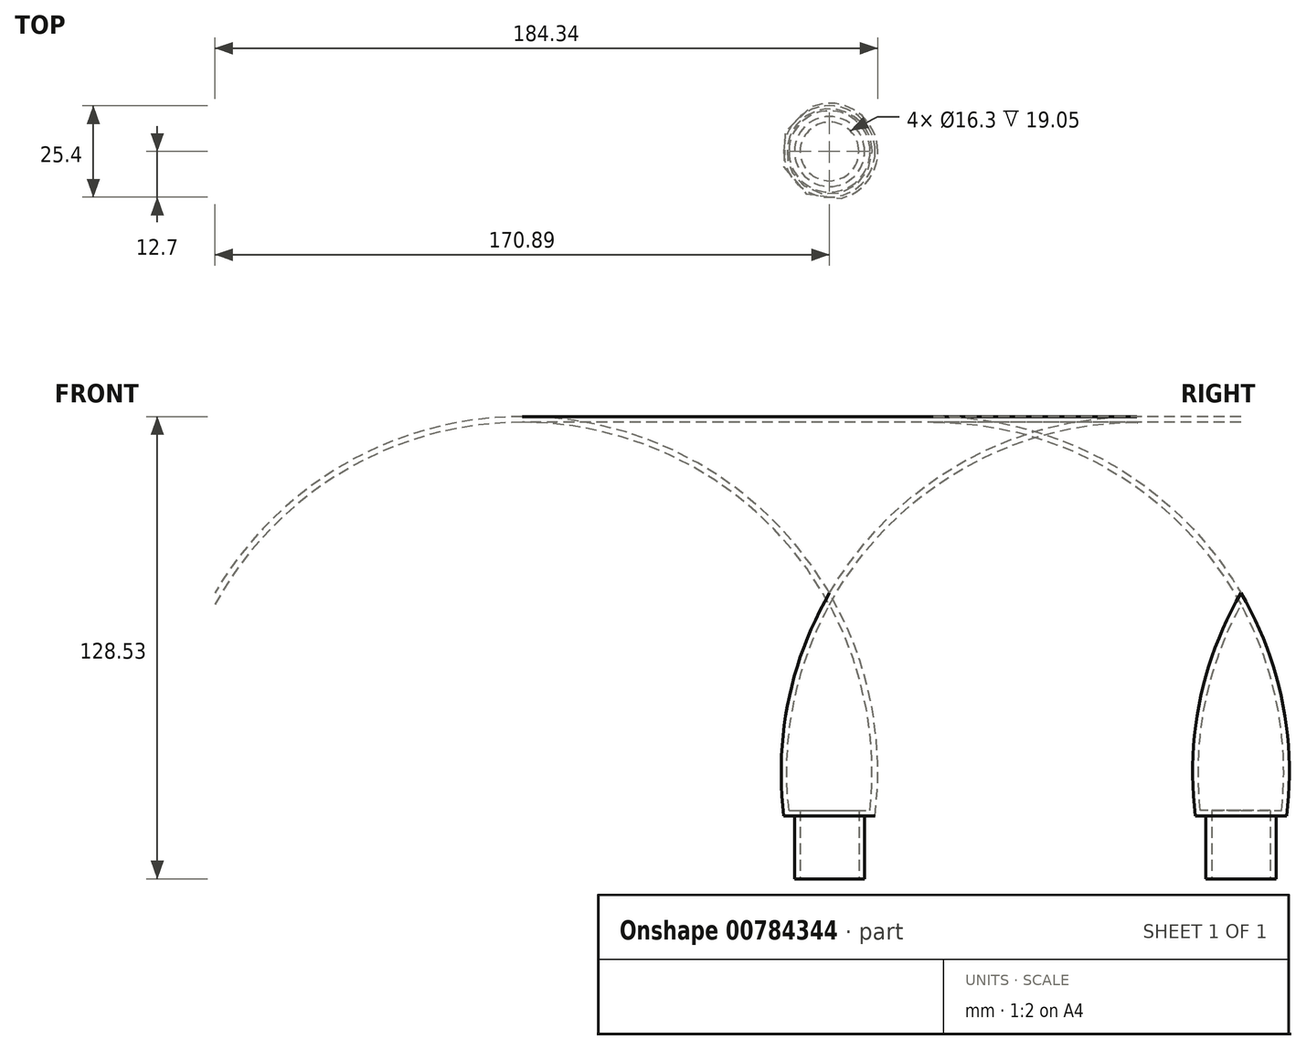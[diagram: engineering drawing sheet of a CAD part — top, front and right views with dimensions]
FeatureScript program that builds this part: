
annotation { "Feature Type Name" : "Feature", "Feature Type Description" : "" }
export const myFeature = defineFeature(function(context is Context, id is Id, definition is map)
    precondition{}
    {
        {
            var Q0;
            Q0=qCreatedBy(makeId("Front.planeOp"),FACE);
            var sketch = newSketch(context, id + "F0", { "sketchPlane" : qUnion([Q0])});
            skLineSegment(sketch, "E0", {"start": v(0, 0) * mm, "end": v(0, 76.2) * mm});
            skLineSegment(sketch, "E1", {"start": v(8.15, 0) * mm, "end": v(8.15, 19.05) * mm});
            skLineSegment(sketch, "E2", {"start": v(8.15, 19.05) * mm, "end": v(11.29, 19.05) * mm});
            skLineSegment(sketch, "E3", {"start": v(0, 76.2) * mm, "end": v(0, 79.43) * mm});
            skArc(sketch, "E4", {"start": v(11.29, 19.05) * mm, "mid": v(10.02, 48.49) * mm, "end": v(0, 76.2) * mm});
            skArc(sketch, "E5.0", {"start": v(12.7, 17.46) * mm, "mid": v(11.44, 49.5) * mm, "end": v(0, 79.43) * mm});
            skLineSegment(sketch, "E5.1", {"start": v(9.74, 17.46) * mm, "end": v(12.7, 17.46) * mm});
            skLineSegment(sketch, "E5.2", {"start": v(9.74, 0) * mm, "end": v(9.74, 17.46) * mm});
            skLineSegment(sketch, "E6", {"start": v(8.15, 0) * mm, "end": v(9.74, 0) * mm});
            skLineSegment(sketch, "E7", {"start": v(0, 0) * mm, "end": v(8.15, 0) * mm});
            skSolve(sketch);
        }
        {
            var Q0;
            Q0=makeQuery(id+"F0.imprint","IMPRINT",FACE,{"disambiguationData":[TD([[makeQuery(id+"F0.imprint","IMPRINT",EDGE,{"derivedFrom":sQuery(id+"F0.wireOp",EDGE,"E1")}),-1.0]])]});
            var Q1;
            Q1=sQuery(id+"F0.wireOp",EDGE,"E0");
            revolve(context, id + "F1", {"surfaceOperationType" : NewSurfaceOperationType.NEW, "entities" : qUnion([Q0]), "axis" : qUnion([Q1]), "revolveType" : RevolveType.FULL});
        }
    });
